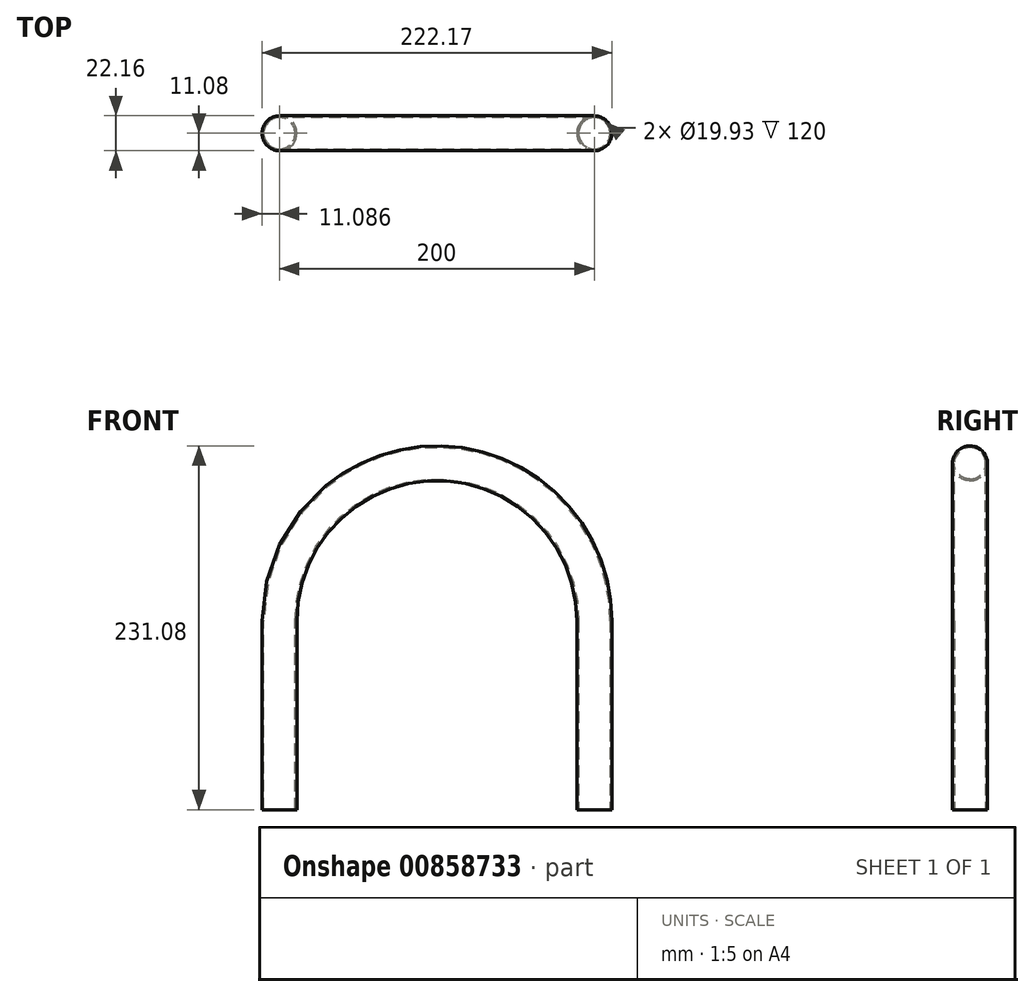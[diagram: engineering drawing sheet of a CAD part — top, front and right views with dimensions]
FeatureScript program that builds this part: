
annotation { "Feature Type Name" : "Feature", "Feature Type Description" : "" }
export const myFeature = defineFeature(function(context is Context, id is Id, definition is map)
    precondition{}
    {
        {
            var Q0;
            Q0=qCreatedBy(makeId("Front.planeOp"),FACE);
            var sketch = newSketch(context, id + "F0", { "sketchPlane" : qUnion([Q0])});
            skLineSegment(sketch, "E0", {"start": v(-89.92, 0) * mm, "end": v(-89.92, 120) * mm});
            skLineSegment(sketch, "E1", {"start": v(110.08, 0) * mm, "end": v(110.08, 120) * mm});
            skArc(sketch, "E2", {"start": v(110.08, 120) * mm, "mid": v(10.08, 220) * mm, "end": v(-89.92, 120) * mm});
            skSolve(sketch);
        }
        {
            var Q0;
            Q0=qCreatedBy(makeId("Top.planeOp"),FACE);
            var sketch = newSketch(context, id + "F1", { "sketchPlane" : qUnion([Q0])});
            skCircle(sketch, "E3", {"center": v(-89.92, 0) * mm, "radius": 11.08 * mm});
            skCircle(sketch, "E4", {"center": v(-89.92, 0) * mm, "radius": 9.96 * mm});
            skSolve(sketch);
        }
        {
            var Q0;
            Q0=makeQuery(id+"F1.imprint","IMPRINT",FACE,{"disambiguationData":[TD([[makeQuery(id+"F1.imprint","IMPRINT",EDGE,{"derivedFrom":sQuery(id+"F1.wireOp",EDGE,"E3")}),1.0]])]});
            var Q1;
            Q1 = qConstructionFilter(qBodyType(qCreatedBy(id + "F0" ,EDGE), BodyType.WIRE), ConstructionObject.NO);
            sweep(context, id + "F2", {"profiles" : qUnion([Q0]), "path" : qUnion([Q1])});
        }
    });
